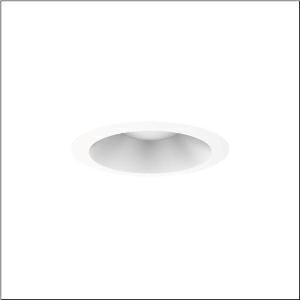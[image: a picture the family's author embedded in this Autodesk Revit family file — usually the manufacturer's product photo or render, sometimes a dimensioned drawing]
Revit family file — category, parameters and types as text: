
# Revit family: lunis_31_midi_51dn15dg32
name_source: partatom
category: Lighting Fixtures
units: mm (PartAtom-declared; Revit-internal decimal feet)

## family parameters
Cut with Voids When Loaded = No
Host = Face
Light Source = No
Part Type = Normal
Room Calculation Point = No
Round Connector Dimension = Use Diameter
Shared = No

## types (1)
- Lunis 31 midi (1 x LED, 2000 lm, 17 W, 3000K)
    Apparent Load = 17 VA
    CIE Flux Codes = 89 99 100 100 100
    Color Rendering = 80
    Color Temperature = 3000K
    Default Elevation = 1800 mm
    Description = Lunis 31,  midi, downlight, light control with lens, light emission: direct distribution, LED rated luminous flux: 2.000lm, light colour: 830, mains connection: 220..240V, AC, 50/60Hz, housing, white, protection rating (complete): IP20, protection rating (on room side): IP54, insulation class (complete): insulation class II (safety insulation), certification: CE, packaging unit: 1 piece
    Height = 0 mm  [stored 0 ft]
    Lamp = 1 x LED
    Lamp Light Flux = 2000 lm
    Lamp Power = 17 W
    Lamp count = 1
    Length = 259 mm
    Luminous efficacy = 118 lm/W
    Manufacturer = Siteco
    ModVariant = No
    Model = 51DN15DG32
    Mounting Place = Ceiling
    Mounting Type = Recessed
    Number of Poles = 1
    OnlyDefault = Yes
    Power Factor = 1
    Product Name = Lunis 31 midi
    Product group = downlight
    ProductGroupID = 400
    Protection Class = Protection class II
    Protection Degree = IP 20
    RLX_Detail_Level = 1
    RLX_Emergency_Light_Flux = 0 lm
    RLX_Emergency_Type = 0
    RLX_Emergency_Type_DB = No
    RlxData = <blob elided: 23689 chars, md5=d359a318>
    Socket = socket
    Standby Power = 0 W
    System Light Flux = 2000 lm
    System Power = 17 W
    Type Comments = Product without accessories
    Type Image = l_1006711.jpg
    URL = http://relux.com
    VarID = ---
    Voltage = 0 V
    Weight = 0.00 kg
    Width = 0 mm  [stored 0 ft]

note: [stored X ft] marks values corroborated as IEEE doubles in the binary element streams (Revit-internal decimal feet)

## geometry (parser evidence)
native form markers: Blend x4, Sweep x12
no freeform markers — native parametric forms only
